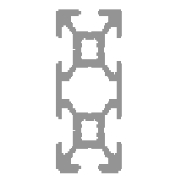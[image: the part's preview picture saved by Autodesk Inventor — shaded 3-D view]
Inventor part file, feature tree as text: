
AUTODESK INVENTOR PART (.ipt)
format: ipt  version: 2023.2 (Build 272271000, 271)  size: 621,056 bytes
history: native  units: mm
features: other x9, sketch x4, reference x2, hole x1, plane x1
ambient origin geometry x8: Origin, YZ Plane, XZ Plane, XY Plane, X Axis, Y Axis, Z Axis, Center Point
bodies: Body (feature_tree)
feature tree (17):
  other  "Driven Length"
  other  "Blocks"
  other  "Start Plane"
  other  "End Plane"
  hole  "Hole1"  [1 undecoded]
  sketch  "Sketch1"  dims[d16=-0.0mm d17=150.0mm]
  other  "20x40"
  sketch  "Sketch10"  dims[d18=0.13mm d19=0.0mm]
  plane  "Work Plane9"
  sketch  "Sketch11"  dims[d20=90.0deg]
  sketch  "Sketch12"  dims[d21=150.0mm d22=5.1mm d23=6.0mm d24=4.0mm d25=2.0mm d26=90.0deg d27=8.0mm d28=20.594885mm]
  reference  "Reference1"
  reference  "Reference2"
  other  "20x40:1"
  parser-record x1  (decoder bookkeeping rows leaked as tree rows — omitted from the tree; the rows remain in map.json)
  other  "Main Assembly.iam"
  other  "X axis motor mount:1"
note: 1 required parameter value undecoded (feature->parameter linkage not recoverable at this tier; creation-order binding heuristic only, values carry confidence <= 0.55)
note: 1 file-system path scrubbed to <path> (originals preserved in map.json)
